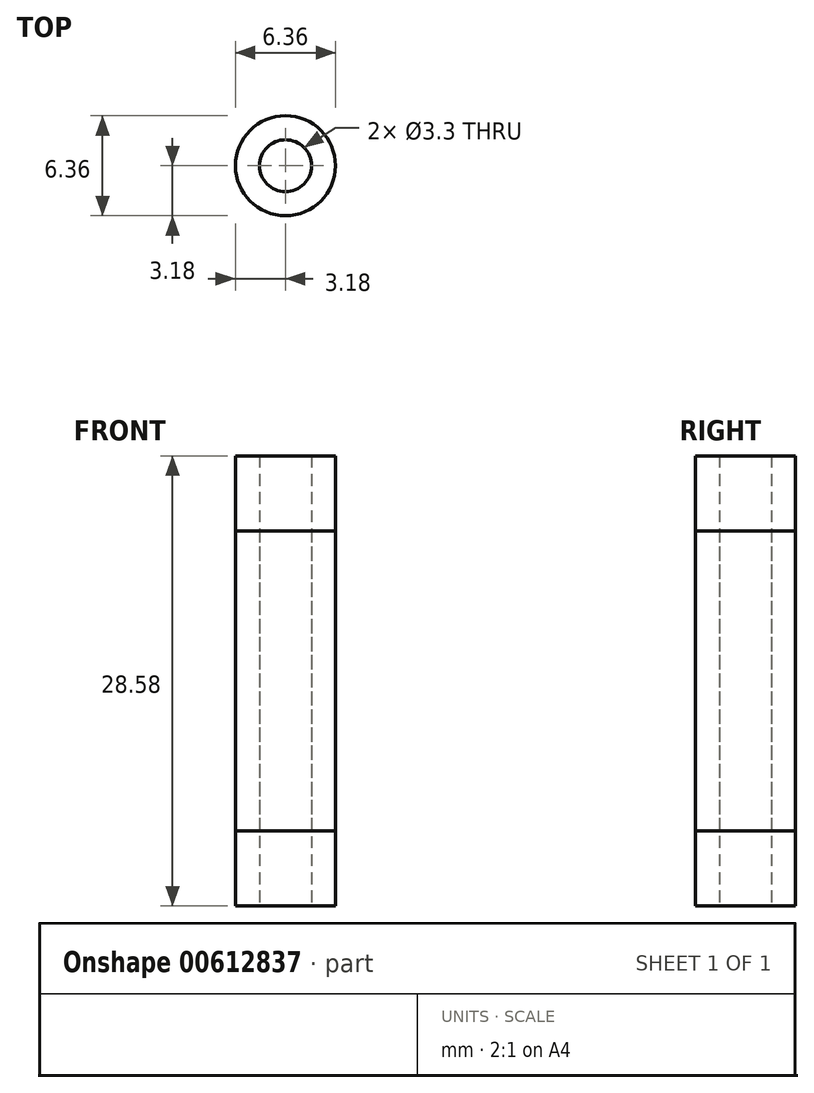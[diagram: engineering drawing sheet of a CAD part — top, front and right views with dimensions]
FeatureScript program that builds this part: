
annotation { "Feature Type Name" : "Feature", "Feature Type Description" : "" }
export const myFeature = defineFeature(function(context is Context, id is Id, definition is map)
    precondition{}
    {
        {
            var Q0;
            Q0=qCreatedBy(makeId("Top.planeOp"),FACE);
            var sketch = newSketch(context, id + "F0", { "sketchPlane" : qUnion([Q0])});
            skCircle(sketch, "E0", {"center": v(0, 0) * mm, "radius": 3.18 * mm});
            skCircle(sketch, "E1", {"center": v(0, 0) * mm, "radius": 1.65 * mm});
            skSolve(sketch);
        }
        {
            var Q0;
            Q0=qSketchRegion(id+"F0",true);
            extrude(context, id + "F1", {"entities" : qUnion([Q0]), "depth" : 28.57 * mm, "symmetric" : true});
        }
        {
            var Q0;
            Q0=qCreatedBy(makeId("Top.planeOp"),FACE);
            var sketch = newSketch(context, id + "F2", { "sketchPlane" : qUnion([Q0])});
            skCircle(sketch, "E2", {"center": v(0, 0) * mm, "radius": 3.18 * mm});
            skCircle(sketch, "E3", {"center": v(0, 0) * mm, "radius": 1.65 * mm});
            skSolve(sketch);
        }
        {
            var Q0;
            Q0=qSketchRegion(id+"F2",true);
            extrude(context, id + "F3", {"entities" : qUnion([Q0]), "depth" : 19.05 * mm, "symmetric" : true});
        }
    });
